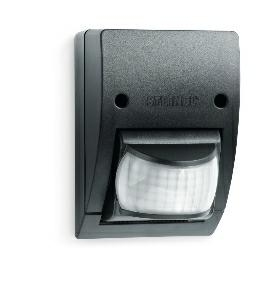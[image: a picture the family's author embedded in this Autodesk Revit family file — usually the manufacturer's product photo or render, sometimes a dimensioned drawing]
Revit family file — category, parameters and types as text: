
# Revit family: is_2160_eco_605919
name_source: partatom
category: Leuchten
revit_build: Autodesk Revit 2016 (Build: 20190508_0715(x64)
units: mm (PartAtom-declared; Revit-internal decimal feet)

## family parameters
Basisbauteil = Fläche
Beim Laden mit Abzugskörper schneiden = Nein
Bemaßung runder Anschluss = Durchmesser verwenden
Gemeinsam genutzt = Nein
Lichtquelle = Nein
Raumberechnungspunkt = Nein
Teiletyp = Normal

## types (1)
- IS 2160 ECO (1 x )
    Beschreibung = Type: Motion detectors; Dimensions (L x W x H): 73 x 78 x 113 mm; Mains power supply: 230 – 240 V / 50 Hz; Sensor Technology: passive infrared; Application, place: Outdoors, Indoors; Application, room: outdoors, front door, all round the building, terrace / balcony, courtyard & driveway; Installation site: wall; Installation: Surface wiring; Switching zones: 260 switching zones; Electronic scalability: No; Mechanical scalability: No; Mounting height: 1,80 – 3,00 m; Optimum mounting height: 2 m; Detection angle: 160 °; Angle of aperture: 40 °; Sneak-by guard: No; Capability of masking out individual segments: Yes; Reach, radial: r = 3 m (13 m²); Reach, tangential: r = 12 m (201 m²); Twilight setting TEACH: No; Twilight setting: 2 – 2000 lx; Time setting: 8 sec – 35 min; Switching output 1, resistive: 600 W; Switching output 1, number of LEDs / fluorescent lamps: 4 pcs.; Constant-lighting control: No; Basic light level function: No; Settings via: Potentiometers; With remote control: No; Interconnection: Yes; IP-rating: IP54; Material: Plastic; Ambient temperature: -20 – 50 °C; Colour: black; Colour, RAL: 9005; IDs, certificates: VDE; Manufacturer's Warranty: 5 years; Version: black; PU1, EAN: 4007841605919
    CIE Flux Codes = 17 43 73 100 2
    Frequency = 50 Hz
    Height = 113 mm
    Hersteller = Steinel
    Lamp count = 1
    Lampe = 1 x
    Length = 73 mm
    Luminous efficacy = 0 lm/W
    ModVariant = Nein
    Modell = 605919
    Mounting Type = Surface mounted
    Number of Poles = 1
    OnlyDefault = Ja
    Power Factor = 1
    Product Name = IS 2160 ECO
    Product group = Sensor-switched indoor light
    ProductGroupID = 30
    Protection Class = Protection class
    Protection Degree = IP 54
    RlxData = <blob elided: 66429 chars, md5=7b3ec7f6>
    Scheinlast = 0 VA
    Socket = socket
    Standby Power = 0 W
    System Light Flux = 0 lm
    System Power = 0 W
    Typenbild = produkt1_605919.jpg
    Typenkommentare = Product without accessories
    URL = http://relux.com
    VarID = ---
    Voltage = 0 V
    Vorgabe-Ansicht = 1800 mm
    Weight = 0.00 kg
    Width = 78 mm  [stored 0.255906 ft]

note: [stored X ft] marks values corroborated as IEEE doubles in the binary element streams (Revit-internal decimal feet)

## geometry (parser evidence)
native form markers: Sweep x7
no freeform markers — native parametric forms only
